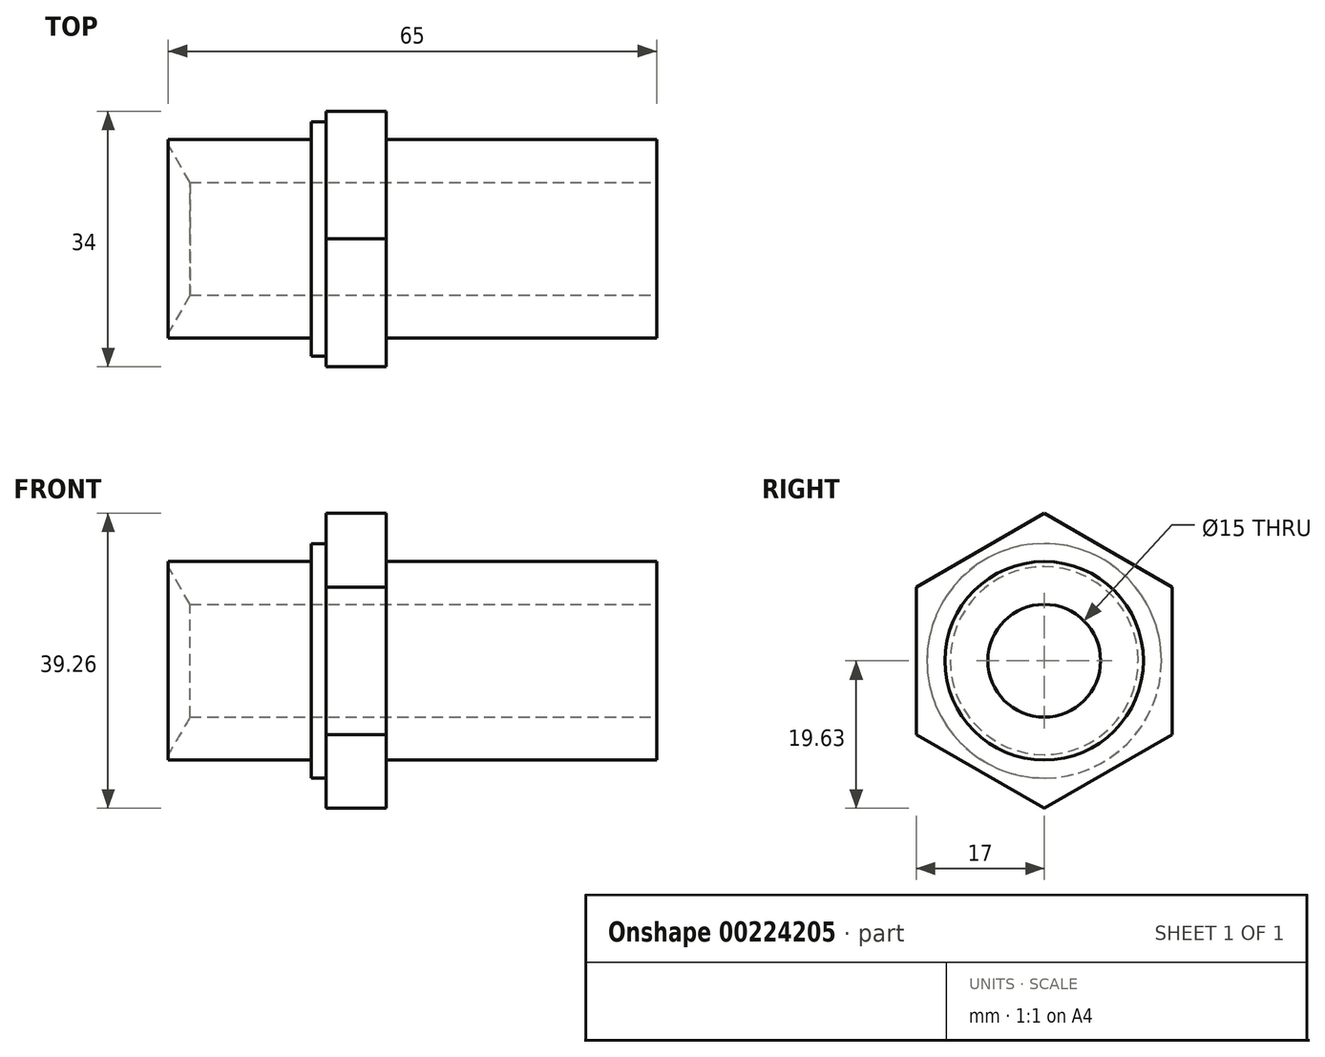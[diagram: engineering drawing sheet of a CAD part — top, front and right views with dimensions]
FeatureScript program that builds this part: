
annotation { "Feature Type Name" : "Feature", "Feature Type Description" : "" }
export const myFeature = defineFeature(function(context is Context, id is Id, definition is map)
    precondition{}
    {
        {
            var Q0;
            Q0=qCreatedBy(makeId("Front.planeOp"),FACE);
            var sketch = newSketch(context, id + "F0", { "sketchPlane" : qUnion([Q0])});
            skLineSegment(sketch, "E0", {"start": v(-29, 0) * mm, "end": v(36, 0) * mm});
            skLineSegment(sketch, "E1", {"start": v(36, 0) * mm, "end": v(36, 13.2) * mm});
            skLineSegment(sketch, "E2", {"start": v(36, 13.2) * mm, "end": v(0, 13.2) * mm});
            skLineSegment(sketch, "E3", {"start": v(0, 13.2) * mm, "end": v(0, 15.6) * mm});
            skLineSegment(sketch, "E4", {"start": v(0, 15.6) * mm, "end": v(-10, 15.6) * mm});
            skLineSegment(sketch, "E5", {"start": v(-10, 15.6) * mm, "end": v(-10, 13.2) * mm});
            skLineSegment(sketch, "E6", {"start": v(-10, 13.2) * mm, "end": v(-29, 13.2) * mm});
            skLineSegment(sketch, "E7", {"start": v(-29, 13.2) * mm, "end": v(-29, 0) * mm});
            skLineSegment(sketch, "E8", {"start": v(-51.42, 0) * mm, "end": v(63.03, 0) * mm, "construction": true});
            skSolve(sketch);
        }
        {
            var Q0;
            Q0 = qSketchRegion(id + "F0", true);
            var Q1;
            Q1=sQuery(id+"F0.wireOp",EDGE,"E8");
            revolve(context, id + "F1", {"entities" : qUnion([Q0]), "axis" : qUnion([Q1]), "revolveType" : RevolveType.FULL});
        }
        {
            var Q0;
            Q0=makeQuery(id+"F1.opRevolve","SWEPT_FACE",FACE,{"disambiguationData":[OSD([sQuery(id+"F0.wireOp",EDGE,"E1")])]});
            var sketch = newSketch(context, id + "F2", { "sketchPlane" : qUnion([Q0])});
            skCircle(sketch, "E9", {"center": v(0, 0) * mm, "radius": 7.5 * mm});
            skSolve(sketch);
        }
        {
            var Q0;
            Q0 = qSketchRegion(id + "F2", true);
            extrude(context, id + "F3", {"entities" : qUnion([Q0]), "operationType" : NewBodyOperationType.REMOVE, "endBound" : BoundingType.THROUGH_ALL, "oppositeDirection" : true, "depth" : 25 * mm});
        }
        {
            var Q0;
            Q0=qCreatedBy(makeId("Right.planeOp"),FACE);
            var sketch = newSketch(context, id + "F4", { "sketchPlane" : qUnion([Q0])});
            skCircle(sketch, "E10.cCircle", {"center": v(0, 0) * mm, "radius": 17 * mm, "construction": true});
            skLineSegment(sketch, "E10.0", {"start": v(-17, -9.81) * mm, "end": v(-17, 9.81) * mm});
            skLineSegment(sketch, "E10.1", {"start": v(-17, 9.81) * mm, "end": v(0, 19.63) * mm});
            skLineSegment(sketch, "E10.2", {"start": v(0, 19.63) * mm, "end": v(17, 9.81) * mm});
            skLineSegment(sketch, "E10.3", {"start": v(17, 9.81) * mm, "end": v(17, -9.81) * mm});
            skLineSegment(sketch, "E10.4", {"start": v(17, -9.81) * mm, "end": v(0, -19.63) * mm});
            skLineSegment(sketch, "E10.5", {"start": v(0, -19.63) * mm, "end": v(-17, -9.81) * mm});
            skPoint(sketch, "E10.0.midPoint", {"position": v(-17, 0) * mm});
            skCircle(sketch, "E11", {"center": v(0, 0) * mm, "radius": 17.5 * mm});
            skCircle(sketch, "E12", {"center": v(0, 0) * mm, "radius": 7.5 * mm});
            skSolve(sketch);
        }
        {
            var Q0;
            {var subQ0=sQuery(id+"F4.wireOp",EDGE,"E11");var subQ1=sQuery(id+"F4.wireOp",EDGE,"E10.0");var subQ18=makeQuery(id+"F4.imprint","INTERSECT",VERTEX,{"disambiguationData":[OD(0.0)],"derivedFrom":[subQ1,subQ0]});Q0=makeQuery(id+"F4.imprint","IMPRINT",FACE,{"disambiguationData":[TD([[makeQuery(id+"F4.imprint","IMPRINT",EDGE,{"disambiguationData":[TD([[subQ18,-1.0]])],"derivedFrom":subQ1}),-1.0]])]});}
            var Q1;
            {var subQ0=sQuery(id+"F4.wireOp",EDGE,"E10.1");var subQ1=sQuery(id+"F4.wireOp",EDGE,"E10.0");var subQ2=makeQuery(id+"F4.imprint","INTERSECT",VERTEX,{"derivedFrom":[subQ1,subQ0]});Q1=makeQuery(id+"F4.imprint","IMPRINT",FACE,{"disambiguationData":[TD([[makeQuery(id+"F4.imprint","IMPRINT",EDGE,{"disambiguationData":[TD([[subQ2,1.0]])],"derivedFrom":subQ1}),-1.0]])]});}
            var Q2;
            {var subQ0=sQuery(id+"F4.wireOp",EDGE,"E10.5");var subQ1=sQuery(id+"F4.wireOp",EDGE,"E10.0");var subQ2=makeQuery(id+"F4.imprint","INTERSECT",VERTEX,{"derivedFrom":[subQ1,subQ0]});Q2=makeQuery(id+"F4.imprint","IMPRINT",FACE,{"disambiguationData":[TD([[makeQuery(id+"F4.imprint","IMPRINT",EDGE,{"disambiguationData":[TD([[subQ2,-1.0]])],"derivedFrom":subQ1}),-1.0]])]});}
            var Q3;
            {var subQ0=sQuery(id+"F4.wireOp",EDGE,"E10.5");var subQ1=sQuery(id+"F4.wireOp",EDGE,"E10.4");var subQ2=makeQuery(id+"F4.imprint","INTERSECT",VERTEX,{"derivedFrom":[subQ1,subQ0]});Q3=makeQuery(id+"F4.imprint","IMPRINT",FACE,{"disambiguationData":[TD([[makeQuery(id+"F4.imprint","IMPRINT",EDGE,{"disambiguationData":[TD([[subQ2,1.0]])],"derivedFrom":subQ1}),-1.0]])]});}
            var Q4;
            {var subQ0=sQuery(id+"F4.wireOp",EDGE,"E10.4");var subQ1=sQuery(id+"F4.wireOp",EDGE,"E10.3");var subQ2=makeQuery(id+"F4.imprint","INTERSECT",VERTEX,{"derivedFrom":[subQ1,subQ0]});Q4=makeQuery(id+"F4.imprint","IMPRINT",FACE,{"disambiguationData":[TD([[makeQuery(id+"F4.imprint","IMPRINT",EDGE,{"disambiguationData":[TD([[subQ2,1.0]])],"derivedFrom":subQ1}),-1.0]])]});}
            var Q5;
            {var subQ0=sQuery(id+"F4.wireOp",EDGE,"E10.3");var subQ1=sQuery(id+"F4.wireOp",EDGE,"E10.2");var subQ2=makeQuery(id+"F4.imprint","INTERSECT",VERTEX,{"derivedFrom":[subQ1,subQ0]});Q5=makeQuery(id+"F4.imprint","IMPRINT",FACE,{"disambiguationData":[TD([[makeQuery(id+"F4.imprint","IMPRINT",EDGE,{"disambiguationData":[TD([[subQ2,1.0]])],"derivedFrom":subQ1}),-1.0]])]});}
            var Q6;
            {var subQ0=sQuery(id+"F4.wireOp",EDGE,"E10.2");var subQ1=sQuery(id+"F4.wireOp",EDGE,"E10.1");var subQ2=makeQuery(id+"F4.imprint","INTERSECT",VERTEX,{"derivedFrom":[subQ1,subQ0]});Q6=makeQuery(id+"F4.imprint","IMPRINT",FACE,{"disambiguationData":[TD([[makeQuery(id+"F4.imprint","IMPRINT",EDGE,{"disambiguationData":[TD([[subQ2,1.0]])],"derivedFrom":subQ1}),-1.0]])]});}
            extrude(context, id + "F5", {"entities" : qUnion([Q0, Q1, Q2, Q3, Q4, Q5, Q6]), "operationType" : NewBodyOperationType.ADD, "oppositeDirection" : true, "depth" : 8 * mm});
        }
        {
            var Q0;
            Q0=makeQuery(id+"F3.boolean.opBoolean","INTERSECT",EDGE,{"derivedFrom":[makeQuery(id+"F1.opRevolve","SWEPT_FACE",FACE,{"disambiguationData":[OSD([sQuery(id+"F0.wireOp",EDGE,"E7")])]}),makeQuery(id+"F3.opExtrude","SWEPT_FACE",FACE,{"disambiguationData":[OSD([sQuery(id+"F2.wireOp",EDGE,"E9")])]})]});
            chamfer(context, id + "F6", {"entities" : qUnion([Q0]), "chamferType" : ChamferType.OFFSET_ANGLE, "width" : 5 * mm, "oppositeDirection" : false, "angle" : 30 * degree, "tangentPropagation" : true});
        }
    });
